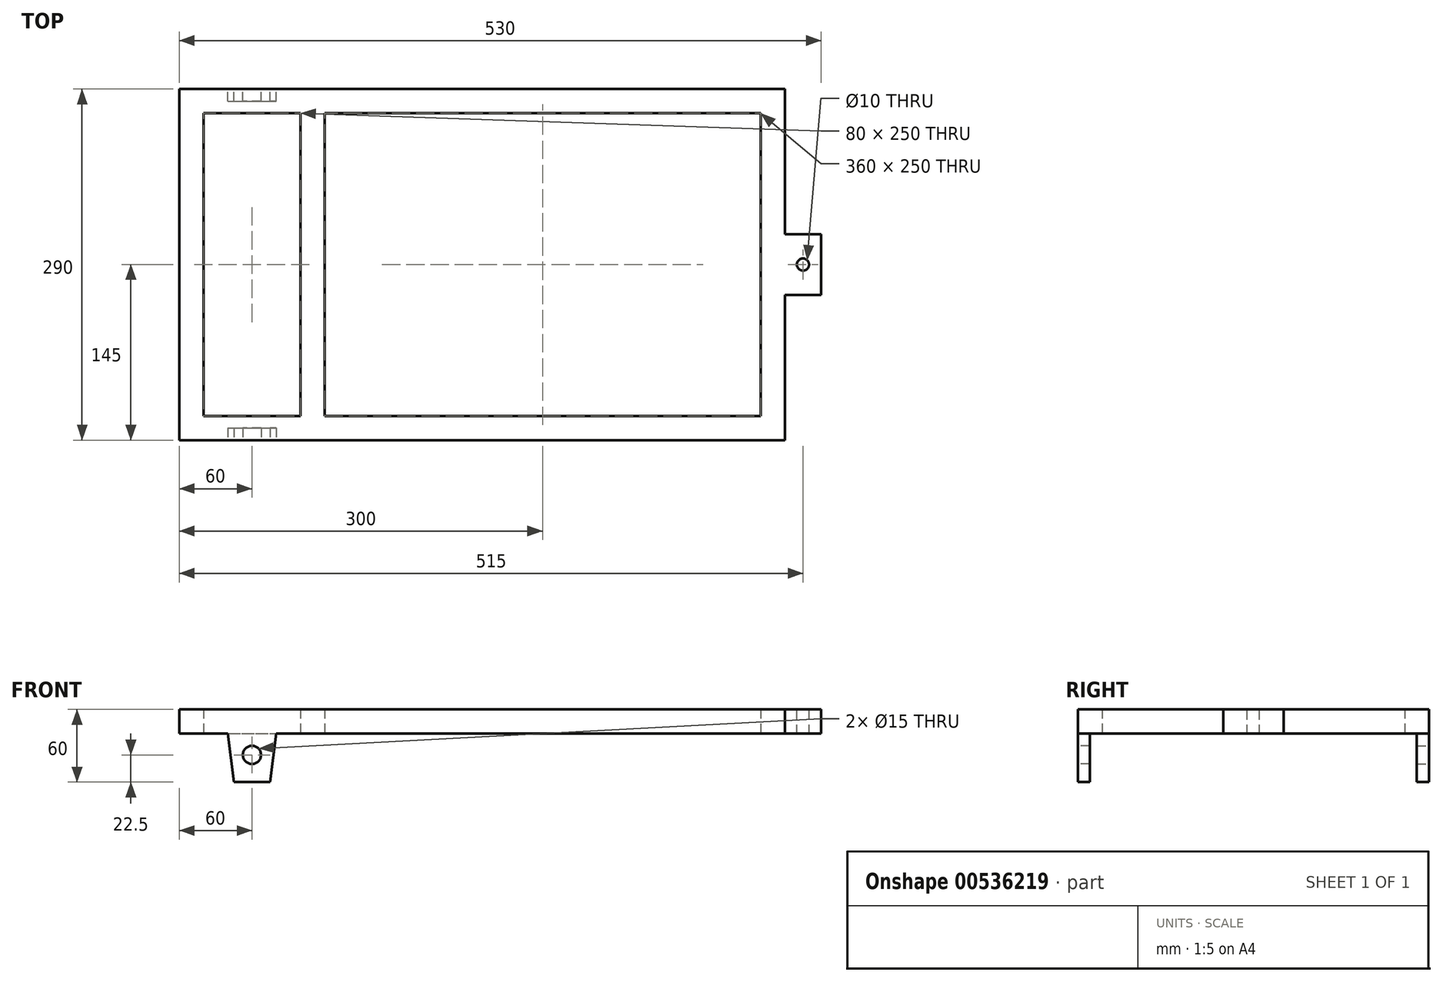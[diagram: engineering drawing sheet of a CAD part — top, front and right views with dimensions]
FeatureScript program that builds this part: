
annotation { "Feature Type Name" : "Feature", "Feature Type Description" : "" }
export const myFeature = defineFeature(function(context is Context, id is Id, definition is map)
    precondition{}
    {
        {
            var Q0;
            Q0=qCreatedBy(makeId("Top.planeOp"),FACE);
            var sketch = newSketch(context, id + "F0", { "sketchPlane" : qUnion([Q0])});
            skLineSegment(sketch, "E0.bottom", {"start": v(200, 145) * mm, "end": v(-200, 145) * mm});
            skLineSegment(sketch, "E0.top", {"start": v(200, -145) * mm, "end": v(-200, -145) * mm});
            skLineSegment(sketch, "E0.left", {"start": v(200, 145) * mm, "end": v(200, -145) * mm});
            skLineSegment(sketch, "E0.right", {"start": v(-200, 145) * mm, "end": v(-200, -145) * mm});
            skPoint(sketch, "E0.middle", {"position": v(0, 0) * mm});
            skLineSegment(sketch, "E1.bottom", {"start": v(180, 125) * mm, "end": v(-180, 125) * mm});
            skLineSegment(sketch, "E1.top", {"start": v(180, -125) * mm, "end": v(-180, -125) * mm});
            skLineSegment(sketch, "E1.left", {"start": v(180, 125) * mm, "end": v(180, -125) * mm});
            skLineSegment(sketch, "E1.right", {"start": v(-180, 125) * mm, "end": v(-180, -125) * mm});
            skSolve(sketch);
        }
        {
            var Q0;
            Q0 = qSketchRegion(id + "F0", true);
            extrude(context, id + "F1", {"entities" : qUnion([Q0]), "depth" : 10 * mm, "offsetDistance" : 25 * mm});
        }
        {
            var Q0;
            Q0=makeQuery(id+"F1.opExtrude","SWEPT_FACE",FACE,{"disambiguationData":[OSD([sQuery(id+"F0.wireOp",EDGE,"E0.left")])]});
            var sketch = newSketch(context, id + "F2", { "sketchPlane" : qUnion([Q0])});
            skLineSegment(sketch, "E2", {"start": v(-145, 5) * mm, "end": v(57.86, 5) * mm, "construction": true});
            skPoint(sketch, "E2.endSnap0", {"position": v(145, 5) * mm});
            skLineSegment(sketch, "E3", {"start": v(0, 0) * mm, "end": v(0, 26.56) * mm, "construction": true});
            skPoint(sketch, "E3.endSnap0", {"position": v(0, 0) * mm});
            skLineSegment(sketch, "E4.bottom", {"start": v(15, 10) * mm, "end": v(-15, 10) * mm});
            skLineSegment(sketch, "E4.top", {"start": v(15, 0) * mm, "end": v(-15, 0) * mm});
            skLineSegment(sketch, "E4.left", {"start": v(15, 10) * mm, "end": v(15, 0) * mm});
            skLineSegment(sketch, "E4.right", {"start": v(-15, 10) * mm, "end": v(-15, 0) * mm});
            skPoint(sketch, "E4.middle", {"position": v(0, 5) * mm});
            skSolve(sketch);
        }
        {
            var Q0;
            Q0 = qSketchRegion(id + "F2", true);
            extrude(context, id + "F3", {"entities" : qUnion([Q0]), "operationType" : NewBodyOperationType.ADD, "depth" : 30 * mm, "offsetDistance" : 25 * mm});
        }
        {
            var Q0;
            Q0=makeQuery(id+"F3.opExtrude","SWEPT_FACE",FACE,{"disambiguationData":[OSD([sQuery(id+"F2.wireOp",EDGE,"E4.bottom")])]});
            var sketch = newSketch(context, id + "F4", { "sketchPlane" : qUnion([Q0])});
            skCircle(sketch, "E5", {"center": v(215, 0) * mm, "radius": 5 * mm});
            skPoint(sketch, "E5.centerSnap0", {"position": v(215, 12.5) * mm});
            skPoint(sketch, "E5.centerSnap1", {"position": v(230, 0) * mm});
            skLineSegment(sketch, "E6", {"start": v(215, 35.42) * mm, "end": v(200, 35.42) * mm, "construction": true});
            skPoint(sketch, "E6.startSnap0", {"position": v(215, 15) * mm});
            skSolve(sketch);
        }
        {
            var Q0;
            Q0=makeQuery(id+"F1.opExtrude","SWEPT_FACE",FACE,{"disambiguationData":[OSD([sQuery(id+"F0.wireOp",EDGE,"E0.right")])]});
            var sketch = newSketch(context, id + "F5", { "sketchPlane" : qUnion([Q0])});
            skLineSegment(sketch, "E7.bottom", {"start": v(-145, 10) * mm, "end": v(-125, 10) * mm});
            skLineSegment(sketch, "E7.top", {"start": v(-145, 0) * mm, "end": v(-125, 0) * mm});
            skLineSegment(sketch, "E7.left", {"start": v(-145, 10) * mm, "end": v(-145, 0) * mm});
            skLineSegment(sketch, "E7.right", {"start": v(-125, 10) * mm, "end": v(-125, 0) * mm});
            skLineSegment(sketch, "E8.bottom", {"start": v(145, 10) * mm, "end": v(125, 10) * mm});
            skLineSegment(sketch, "E8.top", {"start": v(145, 0) * mm, "end": v(125, 0) * mm});
            skLineSegment(sketch, "E8.left", {"start": v(145, 10) * mm, "end": v(145, 0) * mm});
            skLineSegment(sketch, "E8.right", {"start": v(125, 10) * mm, "end": v(125, 0) * mm});
            skSolve(sketch);
        }
        {
            var Q0;
            Q0 = qSketchRegion(id + "F5", true);
            extrude(context, id + "F6", {"entities" : qUnion([Q0]), "operationType" : NewBodyOperationType.ADD, "depth" : 100 * mm, "offsetDistance" : 25 * mm});
        }
        {
            var Q0;
            Q0=makeQuery(id+"F6.opExtrude","SWEPT_FACE",FACE,{"disambiguationData":[OSD([sQuery(id+"F5.wireOp",EDGE,"E7.right")])]});
            var sketch = newSketch(context, id + "F7", { "sketchPlane" : qUnion([Q0])});
            skLineSegment(sketch, "E9.bottom", {"start": v(-300, 10) * mm, "end": v(-280, 10) * mm});
            skLineSegment(sketch, "E9.top", {"start": v(-300, 0) * mm, "end": v(-280, 0) * mm});
            skLineSegment(sketch, "E9.left", {"start": v(-300, 10) * mm, "end": v(-300, 0) * mm});
            skLineSegment(sketch, "E9.right", {"start": v(-280, 10) * mm, "end": v(-280, 0) * mm});
            skSolve(sketch);
        }
        {
            var Q0;
            Q0 = qSketchRegion(id + "F7", true);
            extrude(context, id + "F8", {"entities" : qUnion([Q0]), "operationType" : NewBodyOperationType.ADD, "endBound" : BoundingType.UP_TO_NEXT, "depth" : 25 * mm, "offsetDistance" : 25 * mm});
        }
        {
            var Q0;
            Q0 = qSketchRegion(id + "F4", true);
            extrude(context, id + "F9", {"entities" : qUnion([Q0]), "operationType" : NewBodyOperationType.REMOVE, "oppositeDirection" : true, "depth" : 25 * mm, "offsetDistance" : 25 * mm});
        }
        {
            var Q0;
            Q0=makeQuery(id+"FjvZuM6eGP2HPwx_2.boolean.opBoolean","MERGE",FACE,{"derivedFrom":[makeQuery(id+"FuLaXejFNxQlSqS_2.boolean.opBoolean","MERGE",FACE,{"derivedFrom":[makeQuery(id+"F8.boolean.opBoolean","MERGE",FACE,{"derivedFrom":[makeQuery(id+"F6.boolean.opBoolean","MERGE",FACE,{"derivedFrom":[makeQuery(id+"F3.boolean.opBoolean","MERGE",FACE,{"derivedFrom":[makeQuery(id+"F1.opExtrude","CAP_FACE",FACE,{"disambiguationData":[OSD([sQuery(id+"F0.wireOp",EDGE,"E0.bottom"),sQuery(id+"F0.wireOp",EDGE,"E0.top"),sQuery(id+"F0.wireOp",EDGE,"E0.left"),sQuery(id+"F0.wireOp",EDGE,"E0.right"),sQuery(id+"F0.wireOp",EDGE,"E1.bottom"),sQuery(id+"F0.wireOp",EDGE,"E1.top"),sQuery(id+"F0.wireOp",EDGE,"E1.left"),sQuery(id+"F0.wireOp",EDGE,"E1.right")])],"isStart":false}),makeQuery(id+"F3.opExtrude","SWEPT_FACE",FACE,{"disambiguationData":[OSD([sQuery(id+"F2.wireOp",EDGE,"E4.bottom")])]})]}),makeQuery(id+"F6.opExtrude","SWEPT_FACE",FACE,{"disambiguationData":[OSD([sQuery(id+"F5.wireOp",EDGE,"E7.bottom")])]}),makeQuery(id+"F6.opExtrude","SWEPT_FACE",FACE,{"disambiguationData":[OSD([sQuery(id+"F5.wireOp",EDGE,"E8.bottom")])]})]}),makeQuery(id+"F8.opExtrude","SWEPT_FACE",FACE,{"disambiguationData":[OSD([sQuery(id+"F7.wireOp",EDGE,"E9.bottom")])]})]}),makeQuery(id+"FuLaXejFNxQlSqS_2.opExtrude","SWEPT_FACE",FACE,{"disambiguationData":[OSD([sQuery(id+"FqdVtHyO57hHWNB_2.wireOp",EDGE,"NaEWYZXP-p7j4-ccT0-c0QX-aID1GCMp74EX.bottom")])]})]}),makeQuery(id+"FjvZuM6eGP2HPwx_2.opExtrude","SWEPT_FACE",FACE,{"disambiguationData":[OSD([sQuery(id+"FoUb9VldxoazIi0_2.wireOp",EDGE,"BMDSZXtN-2plk-0971-mxaQ-alm0Zz1ZoPWE.bottom")])]})]});
            var sketch = newSketch(context, id + "F10", { "sketchPlane" : qUnion([Q0])});
            skCircle(sketch, "E10", {"center": v(-70, 35) * mm, "radius": 1.25 * mm});
            skPoint(sketch, "E10.centerSnap0", {"position": v(-70, 30) * mm});
            skCircle(sketch, "E11", {"center": v(-150, 35) * mm, "radius": 1.25 * mm});
            skPoint(sketch, "E11.centerSnap0", {"position": v(-150, 30) * mm});
            skSolve(sketch);
        }
        {
            var Q0;
            Q0 = qSketchRegion(id + "F10", true);
            extrude(context, id + "F11", {"entities" : qUnion([Q0]), "operationType" : NewBodyOperationType.REMOVE, "endBound" : BoundingType.THROUGH_ALL, "oppositeDirection" : true, "depth" : 25 * mm, "offsetDistance" : 25 * mm});
        }
        {
            var Q0;
            Q0=makeQuery(id+"FjvZuM6eGP2HPwx_2.boolean.opBoolean","MERGE",FACE,{"derivedFrom":[makeQuery(id+"FuLaXejFNxQlSqS_2.boolean.opBoolean","MERGE",FACE,{"derivedFrom":[makeQuery(id+"F8.boolean.opBoolean","MERGE",FACE,{"derivedFrom":[makeQuery(id+"F6.boolean.opBoolean","MERGE",FACE,{"derivedFrom":[makeQuery(id+"F3.boolean.opBoolean","MERGE",FACE,{"derivedFrom":[makeQuery(id+"F1.opExtrude","CAP_FACE",FACE,{"disambiguationData":[OSD([sQuery(id+"F0.wireOp",EDGE,"E0.bottom"),sQuery(id+"F0.wireOp",EDGE,"E0.top"),sQuery(id+"F0.wireOp",EDGE,"E0.left"),sQuery(id+"F0.wireOp",EDGE,"E0.right"),sQuery(id+"F0.wireOp",EDGE,"E1.bottom"),sQuery(id+"F0.wireOp",EDGE,"E1.top"),sQuery(id+"F0.wireOp",EDGE,"E1.left"),sQuery(id+"F0.wireOp",EDGE,"E1.right")])],"isStart":false}),makeQuery(id+"F3.opExtrude","SWEPT_FACE",FACE,{"disambiguationData":[OSD([sQuery(id+"F2.wireOp",EDGE,"E4.bottom")])]})]}),makeQuery(id+"F6.opExtrude","SWEPT_FACE",FACE,{"disambiguationData":[OSD([sQuery(id+"F5.wireOp",EDGE,"E7.bottom")])]}),makeQuery(id+"F6.opExtrude","SWEPT_FACE",FACE,{"disambiguationData":[OSD([sQuery(id+"F5.wireOp",EDGE,"E8.bottom")])]})]}),makeQuery(id+"F8.opExtrude","SWEPT_FACE",FACE,{"disambiguationData":[OSD([sQuery(id+"F7.wireOp",EDGE,"E9.bottom")])]})]}),makeQuery(id+"FuLaXejFNxQlSqS_2.opExtrude","SWEPT_FACE",FACE,{"disambiguationData":[OSD([sQuery(id+"FqdVtHyO57hHWNB_2.wireOp",EDGE,"NaEWYZXP-p7j4-ccT0-c0QX-aID1GCMp74EX.bottom")])]})]}),makeQuery(id+"FjvZuM6eGP2HPwx_2.opExtrude","SWEPT_FACE",FACE,{"disambiguationData":[OSD([sQuery(id+"FoUb9VldxoazIi0_2.wireOp",EDGE,"BMDSZXtN-2plk-0971-mxaQ-alm0Zz1ZoPWE.bottom")])]})]});
            var sketch = newSketch(context, id + "F12", { "sketchPlane" : qUnion([Q0])});
            skSolve(sketch);
        }
        {
            var Q0;
            Q0=makeQuery(id+"F8.boolean.opBoolean","MERGE",FACE,{"derivedFrom":[makeQuery(id+"F6.boolean.opBoolean","MERGE",FACE,{"derivedFrom":[makeQuery(id+"F3.boolean.opBoolean","MERGE",FACE,{"derivedFrom":[makeQuery(id+"F1.opExtrude","CAP_FACE",FACE,{"disambiguationData":[OSD([sQuery(id+"F0.wireOp",EDGE,"E0.bottom"),sQuery(id+"F0.wireOp",EDGE,"E0.top"),sQuery(id+"F0.wireOp",EDGE,"E0.left"),sQuery(id+"F0.wireOp",EDGE,"E0.right"),sQuery(id+"F0.wireOp",EDGE,"E1.bottom"),sQuery(id+"F0.wireOp",EDGE,"E1.top"),sQuery(id+"F0.wireOp",EDGE,"E1.left"),sQuery(id+"F0.wireOp",EDGE,"E1.right")])],"isStart":true}),makeQuery(id+"F3.opExtrude","SWEPT_FACE",FACE,{"disambiguationData":[OSD([sQuery(id+"F2.wireOp",EDGE,"E4.top")])]})]}),makeQuery(id+"F6.opExtrude","SWEPT_FACE",FACE,{"disambiguationData":[OSD([sQuery(id+"F5.wireOp",EDGE,"E7.top")])]}),makeQuery(id+"F6.opExtrude","SWEPT_FACE",FACE,{"disambiguationData":[OSD([sQuery(id+"F5.wireOp",EDGE,"E8.top")])]})]}),makeQuery(id+"F8.opExtrude","SWEPT_FACE",FACE,{"disambiguationData":[OSD([sQuery(id+"F7.wireOp",EDGE,"E9.top")])]})]});
            var sketch = newSketch(context, id + "F13", { "sketchPlane" : qUnion([Q0])});
            skLineSegment(sketch, "E12", {"start": v(-240, -125) * mm, "end": v(-240, 125) * mm, "construction": true});
            skLineSegment(sketch, "E13.bottom", {"start": v(-220, -125) * mm, "end": v(-260, -125) * mm});
            skLineSegment(sketch, "E13.top", {"start": v(-220, -135) * mm, "end": v(-260, -135) * mm});
            skLineSegment(sketch, "E13.left", {"start": v(-220, -125) * mm, "end": v(-220, -135) * mm});
            skLineSegment(sketch, "E13.right", {"start": v(-260, -125) * mm, "end": v(-260, -135) * mm});
            skPoint(sketch, "E13.middle", {"position": v(-240, -130) * mm});
            skSolve(sketch);
        }
        {
            var Q0;
            Q0 = qSketchRegion(id + "F13", true);
            extrude(context, id + "F14", {"entities" : qUnion([Q0]), "depth" : 40 * mm, "offsetDistance" : 25 * mm});
        }
        {
            var Q0;
            Q0=makeQuery(id+"F14.opExtrude","SWEPT_FACE",FACE,{"disambiguationData":[OSD([sQuery(id+"F13.wireOp",EDGE,"E13.top")])]});
            var sketch = newSketch(context, id + "F15", { "sketchPlane" : qUnion([Q0])});
            skLineSegment(sketch, "E14", {"start": v(240, 0) * mm, "end": v(240, -17.5) * mm, "construction": true});
            skCircle(sketch, "E15", {"center": v(240, -17.5) * mm, "radius": 7.5 * mm});
            skLineSegment(sketch, "E16", {"start": v(240, -40) * mm, "end": v(225, -40) * mm});
            skLineSegment(sketch, "E17", {"start": v(240, -40) * mm, "end": v(255, -40) * mm});
            skLineSegment(sketch, "E18", {"start": v(255, -40) * mm, "end": v(260, 0) * mm});
            skLineSegment(sketch, "E19", {"start": v(225, -40) * mm, "end": v(220, 0) * mm});
            skLineSegment(sketch, "E20", {"start": v(232.5, -17.5) * mm, "end": v(276.02, -17.5) * mm, "construction": true});
            skLineSegment(sketch, "E21", {"start": v(276.02, -17.5) * mm, "end": v(276.02, 0) * mm, "construction": true});
            skSolve(sketch);
        }
        {
            var Q0;
            Q0 = qSketchRegion(id + "F15", true);
            var Q1;
            {var subQ0=sQuery(id+"F15.wireOp",EDGE,"E19");Q1=makeQuery(id+"F15.imprint","IMPRINT",FACE,{"disambiguationData":[TD([[makeQuery(id+"F15.imprint","IMPRINT",EDGE,{"derivedFrom":subQ0}),1.0]])]});}
            var Q2;
            {var subQ0=sQuery(id+"F15.wireOp",EDGE,"E18");Q2=makeQuery(id+"F15.imprint","IMPRINT",FACE,{"disambiguationData":[TD([[makeQuery(id+"F15.imprint","IMPRINT",EDGE,{"derivedFrom":subQ0}),-1.0]])]});}
            extrude(context, id + "F16", {"entities" : qUnion([Q0, Q1, Q2]), "operationType" : NewBodyOperationType.REMOVE, "endBound" : BoundingType.THROUGH_ALL, "oppositeDirection" : true, "depth" : 25 * mm, "offsetDistance" : 25 * mm});
        }
        {
            var Q0;
            Q0=makeQuery(id+"F14.opExtrude","SWEPT_BODY",BODY,{"disambiguationData":[OSD([sQuery(id+"F13.wireOp",EDGE,"E13.bottom"),sQuery(id+"F13.wireOp",EDGE,"E13.top"),sQuery(id+"F13.wireOp",EDGE,"E13.left"),sQuery(id+"F13.wireOp",EDGE,"E13.right")])]});
            var Q1;
            Q1=qCreatedBy(makeId("Front.planeOp"),FACE);
            mirror(context, id + "F17", {"operationType" : NewBodyOperationType.ADD, "entities" : qUnion([Q0]), "mirrorPlane" : qUnion([Q1])});
        }
        {
            var Q0;
            Q0=makeQuery(id+"F3.opExtrude","SWEPT_FACE",FACE,{"disambiguationData":[OSD([sQuery(id+"F2.wireOp",EDGE,"E4.right")])]});
            extrude(context, id + "F18", {"entities" : qUnion([Q0]), "operationType" : NewBodyOperationType.ADD, "depth" : 10 * mm, "offsetDistance" : 25 * mm});
        }
        {
            var Q0;
            Q0=makeQuery(id+"F3.opExtrude","SWEPT_FACE",FACE,{"disambiguationData":[OSD([sQuery(id+"F2.wireOp",EDGE,"E4.left")])]});
            var sketch = newSketch(context, id + "F19", { "sketchPlane" : qUnion([Q0])});
            skSolve(sketch);
        }
        {
            var Q0;
            Q0 = qSketchRegion(id + "F19", true);
            var Q1;
            {var subQ0=sQuery(id+"F2.wireOp",EDGE,"E4.left");Q1=makeQuery(id+"F19.imprint","IMPRINT",FACE,{"disambiguationData":[TD([[makeQuery(id+"F19.imprint","IMPRINT",EDGE,{"derivedFrom":makeQuery(id+"F3.opExtrude","CAP_EDGE",EDGE,{"disambiguationData":[OSD([subQ0])],"isStart":false})}),1.0]])]});}
            extrude(context, id + "F20", {"entities" : qUnion([Q0, Q1]), "operationType" : NewBodyOperationType.ADD, "depth" : 10 * mm, "offsetDistance" : 25 * mm});
        }
        {
            var Q0;
            {var subQ10=sQuery(id+"F0.wireOp",EDGE,"E1.bottom");Q0=makeQuery(id+"F12.imprint","IMPRINT",FACE,{"disambiguationData":[TD([[makeQuery(id+"F12.imprint","IMPRINT",EDGE,{"derivedFrom":makeQuery(id+"F1.opExtrude","CAP_EDGE",EDGE,{"disambiguationData":[OSD([subQ10])],"isStart":false})}),-1.0]])]});}
            var Q1;
            {var subQ0=sQuery(id+"F2.wireOp",EDGE,"E4.bottom");var subQ1=sQuery(id+"F0.wireOp",EDGE,"E0.left");Q1=makeQuery(id+"F20.boolean.opBoolean","MERGE",FACE,{"derivedFrom":[makeQuery(id+"F18.boolean.opBoolean","MERGE",FACE,{"derivedFrom":[makeQuery(id+"F8.boolean.opBoolean","MERGE",FACE,{"derivedFrom":[makeQuery(id+"F6.boolean.opBoolean","MERGE",FACE,{"derivedFrom":[makeQuery(id+"F3.boolean.opBoolean","MERGE",FACE,{"derivedFrom":[makeQuery(id+"F1.opExtrude","CAP_FACE",FACE,{"disambiguationData":[OSD([sQuery(id+"F0.wireOp",EDGE,"E0.bottom"),sQuery(id+"F0.wireOp",EDGE,"E0.top"),subQ1,sQuery(id+"F0.wireOp",EDGE,"E0.right"),sQuery(id+"F0.wireOp",EDGE,"E1.bottom"),sQuery(id+"F0.wireOp",EDGE,"E1.top"),sQuery(id+"F0.wireOp",EDGE,"E1.left"),sQuery(id+"F0.wireOp",EDGE,"E1.right")])],"isStart":false}),makeQuery(id+"F3.opExtrude","SWEPT_FACE",FACE,{"disambiguationData":[OSD([subQ0])]})]}),makeQuery(id+"F6.opExtrude","SWEPT_FACE",FACE,{"disambiguationData":[OSD([sQuery(id+"F5.wireOp",EDGE,"E7.bottom")])]}),makeQuery(id+"F6.opExtrude","SWEPT_FACE",FACE,{"disambiguationData":[OSD([sQuery(id+"F5.wireOp",EDGE,"E8.bottom")])]})]}),makeQuery(id+"F8.opExtrude","SWEPT_FACE",FACE,{"disambiguationData":[OSD([sQuery(id+"F7.wireOp",EDGE,"E9.bottom")])]})]}),makeQuery(id+"F18.opExtrude","SWEPT_FACE",FACE,{"disambiguationData":[OSD([subQ1,subQ0,sQuery(id+"F2.wireOp",EDGE,"E4.right")])]})]}),makeQuery(id+"F20.opExtrude","SWEPT_FACE",FACE,{"disambiguationData":[OSD([subQ1,subQ0,sQuery(id+"F2.wireOp",EDGE,"E4.left")])]})]});}
            extrude(context, id + "F21", {"entities" : qUnion([Q0, Q1]), "operationType" : NewBodyOperationType.ADD, "depth" : 10 * mm, "offsetDistance" : 25 * mm});
        }
        {
            var Q0;
            Q0=makeQuery(id+"F17.opPattern","COPY",FACE,{"derivedFrom":makeQuery(id+"F14.opExtrude","SWEPT_FACE",FACE,{"disambiguationData":[OSD([sQuery(id+"F13.wireOp",EDGE,"E13.top")])]}),"instanceName":"1"});
            var Q1;
            {var subQ0=sQuery(id+"F5.wireOp",EDGE,"E8.left");var subQ1=sQuery(id+"F5.wireOp",EDGE,"E8.bottom");var subQ2=sQuery(id+"F0.wireOp",EDGE,"E0.top");Q1=makeQuery(id+"F21.boolean.opBoolean","MERGE",FACE,{"derivedFrom":[makeQuery(id+"F6.boolean.opBoolean","MERGE",FACE,{"derivedFrom":[makeQuery(id+"F1.opExtrude","SWEPT_FACE",FACE,{"disambiguationData":[OSD([subQ2])]}),makeQuery(id+"F6.opExtrude","SWEPT_FACE",FACE,{"disambiguationData":[OSD([subQ0])]})]}),makeQuery(id+"F21.opExtrude","SWEPT_FACE",FACE,{"disambiguationData":[OSD([subQ2,subQ1,subQ0]),TDD([makeQuery(id+"F12.imprint","IMPRINT",EDGE,{"derivedFrom":makeQuery(id+"F6.boolean.opBoolean","MERGE",EDGE,{"derivedFrom":[makeQuery(id+"F1.opExtrude","CAP_EDGE",EDGE,{"disambiguationData":[OSD([subQ2])],"isStart":false}),makeQuery(id+"F6.opExtrude","SWEPT_EDGE",EDGE,{"disambiguationData":[OSD([subQ1,subQ0])]})]})})])]})]});}
            extrude(context, id + "F22", {"entities" : qUnion([Q0]), "operationType" : NewBodyOperationType.ADD, "endBound" : BoundingType.UP_TO_SURFACE, "depth" : 25 * mm, "endBoundEntityFace" : qUnion([Q1]), "offsetDistance" : 25 * mm});
        }
        {
            var Q0;
            Q0=makeQuery(id+"F14.opExtrude","SWEPT_FACE",FACE,{"disambiguationData":[OSD([sQuery(id+"F13.wireOp",EDGE,"E13.top")])]});
            var Q1;
            {var subQ0=sQuery(id+"F5.wireOp",EDGE,"E7.left");var subQ1=sQuery(id+"F5.wireOp",EDGE,"E7.bottom");var subQ2=sQuery(id+"F0.wireOp",EDGE,"E0.bottom");Q1=makeQuery(id+"F21.boolean.opBoolean","MERGE",FACE,{"derivedFrom":[makeQuery(id+"F6.boolean.opBoolean","MERGE",FACE,{"derivedFrom":[makeQuery(id+"F1.opExtrude","SWEPT_FACE",FACE,{"disambiguationData":[OSD([subQ2])]}),makeQuery(id+"F6.opExtrude","SWEPT_FACE",FACE,{"disambiguationData":[OSD([subQ0])]})]}),makeQuery(id+"F21.opExtrude","SWEPT_FACE",FACE,{"disambiguationData":[OSD([subQ2,subQ1,subQ0]),TDD([makeQuery(id+"F12.imprint","IMPRINT",EDGE,{"derivedFrom":makeQuery(id+"F6.boolean.opBoolean","MERGE",EDGE,{"derivedFrom":[makeQuery(id+"F1.opExtrude","CAP_EDGE",EDGE,{"disambiguationData":[OSD([subQ2])],"isStart":false}),makeQuery(id+"F6.opExtrude","SWEPT_EDGE",EDGE,{"disambiguationData":[OSD([subQ1,subQ0])]})]})})])]})]});}
            extrude(context, id + "F23", {"entities" : qUnion([Q0]), "operationType" : NewBodyOperationType.ADD, "endBound" : BoundingType.UP_TO_SURFACE, "depth" : 25 * mm, "endBoundEntityFace" : qUnion([Q1]), "offsetDistance" : 25 * mm});
        }
        {
            var Q0;
            {var subQ0=sQuery(id+"F5.wireOp",EDGE,"E8.right");var subQ1=sQuery(id+"F5.wireOp",EDGE,"E8.bottom");var subQ2=sQuery(id+"F0.wireOp",EDGE,"E0.right");Q0=makeQuery(id+"F21.boolean.opBoolean","MERGE",FACE,{"derivedFrom":[makeQuery(id+"F17.boolean.opBoolean","MERGE",FACE,{"derivedFrom":[makeQuery(id+"F6.opExtrude","SWEPT_FACE",FACE,{"disambiguationData":[OSD([subQ0])]}),makeQuery(id+"F17.opPattern","COPY",FACE,{"derivedFrom":makeQuery(id+"F14.opExtrude","SWEPT_FACE",FACE,{"disambiguationData":[OSD([sQuery(id+"F13.wireOp",EDGE,"E13.bottom")])]}),"instanceName":"1"})]}),makeQuery(id+"F21.opExtrude","SWEPT_FACE",FACE,{"disambiguationData":[OSD([subQ2,subQ1,subQ0]),TDD([makeQuery(id+"F12.imprint","IMPRINT",EDGE,{"derivedFrom":makeQuery(id+"F6.opExtrude","SWEPT_EDGE",EDGE,{"disambiguationData":[OSD([subQ2,subQ1,subQ0])]})})])]})]});}
            var sketch = newSketch(context, id + "F24", { "sketchPlane" : qUnion([Q0])});
            skLineSegment(sketch, "E22", {"start": v(260, 0) * mm, "end": v(220, 0) * mm});
            skSolve(sketch);
        }
        {
            var Q0;
            Q0 = qSketchRegion(id + "F24", true);
            var Q1;
            Q1=makeQuery(id+"F24.imprint","IMPRINT",FACE,{"disambiguationData":[TD([[makeQuery(id+"F24.imprint","IMPRINT",EDGE,{"derivedFrom":sQuery(id+"F24.wireOp",EDGE,"E22")}),1.0]])]});
            extrude(context, id + "F25", {"entities" : qUnion([Q0, Q1]), "operationType" : NewBodyOperationType.REMOVE, "oppositeDirection" : true, "depth" : 10 * mm, "offsetDistance" : 25 * mm});
        }
        {
            var Q0;
            {var subQ0=sQuery(id+"F5.wireOp",EDGE,"E7.right");var subQ1=sQuery(id+"F5.wireOp",EDGE,"E7.bottom");var subQ2=sQuery(id+"F0.wireOp",EDGE,"E0.right");Q0=makeQuery(id+"F21.boolean.opBoolean","MERGE",FACE,{"derivedFrom":[makeQuery(id+"F17.boolean.opBoolean","MERGE",FACE,{"derivedFrom":[makeQuery(id+"F6.opExtrude","SWEPT_FACE",FACE,{"disambiguationData":[OSD([subQ0])]}),makeQuery(id+"F14.opExtrude","SWEPT_FACE",FACE,{"disambiguationData":[OSD([sQuery(id+"F13.wireOp",EDGE,"E13.bottom")])]})]}),makeQuery(id+"F21.opExtrude","SWEPT_FACE",FACE,{"disambiguationData":[OSD([subQ2,subQ1,subQ0]),TDD([makeQuery(id+"F12.imprint","IMPRINT",EDGE,{"derivedFrom":makeQuery(id+"F6.opExtrude","SWEPT_EDGE",EDGE,{"disambiguationData":[OSD([subQ2,subQ1,subQ0])]})})])]})]});}
            var sketch = newSketch(context, id + "F26", { "sketchPlane" : qUnion([Q0])});
            skLineSegment(sketch, "E23", {"start": v(-260, 0) * mm, "end": v(-220, 0) * mm});
            skSolve(sketch);
        }
        {
            var Q0;
            Q0 = qSketchRegion(id + "F26", true);
            var Q1;
            Q1=makeQuery(id+"F26.imprint","IMPRINT",FACE,{"disambiguationData":[TD([[makeQuery(id+"F26.imprint","IMPRINT",EDGE,{"derivedFrom":sQuery(id+"F26.wireOp",EDGE,"E23")}),-1.0]])]});
            extrude(context, id + "F27", {"entities" : qUnion([Q0, Q1]), "operationType" : NewBodyOperationType.REMOVE, "oppositeDirection" : true, "depth" : 10 * mm, "offsetDistance" : 25 * mm});
        }
    });
